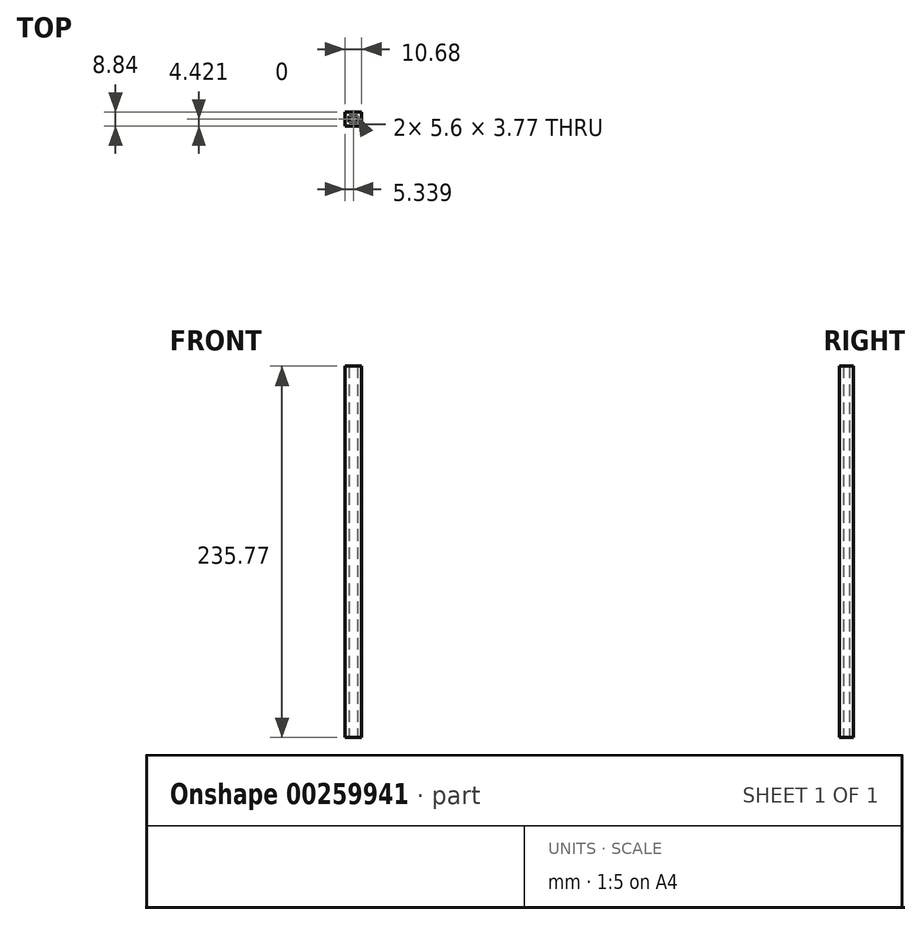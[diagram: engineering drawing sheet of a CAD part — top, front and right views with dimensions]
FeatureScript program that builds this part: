
annotation { "Feature Type Name" : "Feature", "Feature Type Description" : "" }
export const myFeature = defineFeature(function(context is Context, id is Id, definition is map)
    precondition{}
    {
        {
            var Q0;
            Q0=qCreatedBy(makeId("Top.planeOp"),FACE);
            var sketch = newSketch(context, id + "F0", { "sketchPlane" : qUnion([Q0])});
            skLineSegment(sketch, "E0.bottom", {"start": v(-32.9, 39.82) * mm, "end": v(-22.2, 39.82) * mm});
            skLineSegment(sketch, "E0.top", {"start": v(-32.9, 48.66) * mm, "end": v(-22.2, 48.66) * mm});
            skLineSegment(sketch, "E0.left", {"start": v(-32.9, 39.82) * mm, "end": v(-32.9, 48.66) * mm});
            skLineSegment(sketch, "E0.right", {"start": v(-22.2, 39.82) * mm, "end": v(-22.2, 48.66) * mm});
            skSolve(sketch);
        }
        {
            var Q0;
            Q0=makeQuery(id+"F0.imprint","IMPRINT",FACE,{"disambiguationData":[TD([[makeQuery(id+"F0.imprint","IMPRINT",EDGE,{"derivedFrom":sQuery(id+"F0.wireOp",EDGE,"E0.bottom")}),1.0]])]});
            extrude(context, id + "F1", {"entities" : qUnion([Q0]), "depth" : 235.77 * mm});
        }
        {
            var Q0;
            Q0=makeQuery(id+"F1.opExtrude","CAP_FACE",FACE,{"disambiguationData":[OSD([sQuery(id+"F0.wireOp",EDGE,"E0.bottom"),sQuery(id+"F0.wireOp",EDGE,"E0.top"),sQuery(id+"F0.wireOp",EDGE,"E0.left"),sQuery(id+"F0.wireOp",EDGE,"E0.right")])],"isStart":false});
            var Q1;
            Q1=makeQuery(id+"F1.opExtrude","CAP_FACE",FACE,{"disambiguationData":[OSD([sQuery(id+"F0.wireOp",EDGE,"E0.bottom"),sQuery(id+"F0.wireOp",EDGE,"E0.top"),sQuery(id+"F0.wireOp",EDGE,"E0.left"),sQuery(id+"F0.wireOp",EDGE,"E0.right")])],"isStart":true});
            shell(context, id + "F2", {"entities" : qUnion([Q0, Q1]), "thickness" : 2.54 * mm});
        }
    });
